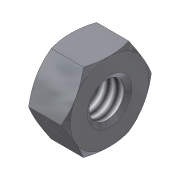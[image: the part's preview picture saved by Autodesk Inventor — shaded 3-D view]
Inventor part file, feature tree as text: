
AUTODESK INVENTOR PART (.ipt)
format: ipt  version: 2015 SP1 (Build 190203100, 203)  size: 148,480 bytes
history: native  units: mm (DEFAULTED — no unit token found)
features: sketch x3, chamfer x1, hole x1
ambient origin geometry x8: Origin, YZ Plane, XZ Plane, XY Plane, X Axis, Y Axis, Z Axis, Center Point
bodies: Solid1 (feature_tree), Body (feature_tree)
feature tree (5):
  chamfer  "Chamfer1"  Angle=30.0deg  [1 undecoded]
  hole  "Thread"  [1 undecoded]
  sketch  "Sketch1"  dims[d0=12.83161mm]
  sketch  "Sketch2"  dims[d1=5.5626mm]
  sketch  "Sketch3"  dims[d2=0.0mm d3=30.0deg d4=30.0deg d5=11.1125mm d6=11.1125mm d7=90.0deg d25=4.9784mm d26=6.0mm d27=4.0mm d28=2.0mm d29=14.3117mm d30=8.0mm d31=20.594885mm d8=0.687408mm d9=30.0deg d10=0.687408mm d11=30.0deg d13=0.0mm d14=0.0mm d39=0.0mm d40=0.687408mm d41=0.687408mm]
note: 2 required parameter values undecoded (feature->parameter linkage not recoverable at this tier; creation-order binding heuristic only, values carry confidence <= 0.55)
